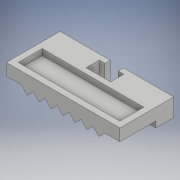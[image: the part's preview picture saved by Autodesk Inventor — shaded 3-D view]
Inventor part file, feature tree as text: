
AUTODESK INVENTOR PART (.ipt)
format: ipt  version: 2017 (Build 210142000, 142)  size: 231,936 bytes
history: native  units: mm
features: extrude x6, sketch x5, chamfer x1, other x1, projected_geometry x1
ambient origin geometry x8: Origin, YZ Plane, XZ Plane, XY Plane, X Axis, Y Axis, Z Axis, Center Point
bodies: Solid1 (feature_tree)
feature tree (14):
  extrude  "Extrusion1"  Depth=9.0mm
  extrude  "Extrusion8"  Depth=1.0mm
  extrude  "Extrusion9"  TaperAngle=135.0deg  [1 undecoded]
  extrude  "Extrusion10"  Depth=4.0mm TaperAngle=0.0deg
  extrude  "Extrusion11"  Depth=2.0mm
  extrude  "Extrusion12"  Depth=2.0mm
  chamfer  "Chamfer1"  Distance=6.0mm
  other  "WeightSection-5mm"
  sketch  "Sketch1"  dims[d0=19.0mm d1=9.0mm]
  sketch  "Sketch11"  dims[d2=3.0mm d3=0.0mm d23=1.0mm]
  sketch  "Sketch12"  dims[d24=6.0mm d25=135.0deg]
  sketch  "Sketch13"  dims[d26=90.0deg d27=4.0mm d28=0.0mm]
  projected_geometry  "Projected Loop4"
  sketch  "Sketch14"  dims[d30=135.0deg d31=40.0mm d33=2.0mm d34=10.0mm d36=10.0mm d38=40.0mm d40=2.0mm d41=10.0mm d43=10.0mm d45=6.0mm d46=0.0mm d47=2.0mm d48=4.1mm d49=2.2mm d50=2.2mm d51=10.0mm d52=0.0mm d53=17.0mm d54=4.0mm d55=1.0mm d56=0.0mm d57=6.0mm d58=1.0mm d59=3.5mm d60=1.0mm d61=0.0mm d62=0.5mm d63=2.0mm d64=45.0deg d65=5.0mm]
note: 1 required parameter value undecoded (feature->parameter linkage not recoverable at this tier; creation-order binding heuristic only, values carry confidence <= 0.55)
